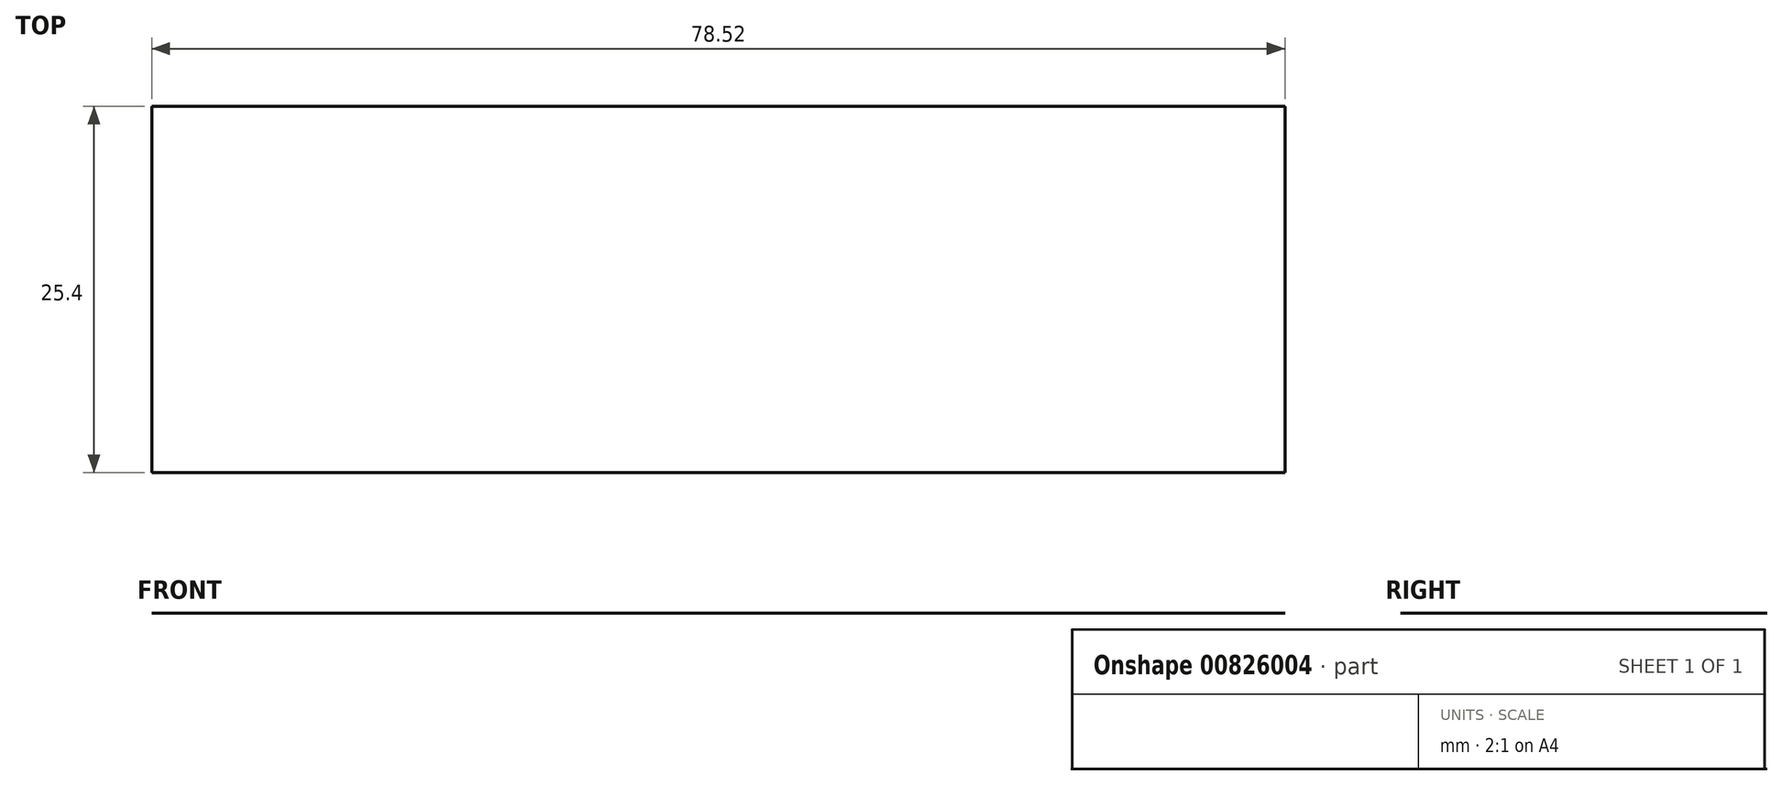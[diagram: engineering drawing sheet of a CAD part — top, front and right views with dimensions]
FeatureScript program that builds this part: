
annotation { "Feature Type Name" : "Feature", "Feature Type Description" : "" }
export const myFeature = defineFeature(function(context is Context, id is Id, definition is map)
    precondition{}
    {
        {
            var Q0;
            Q0=qCreatedBy(makeId("Front.planeOp"),FACE);
            var sketch = newSketch(context, id + "F0", { "sketchPlane" : qUnion([Q0])});
            skLineSegment(sketch, "E0.bottom", {"start": v(0, 0) * mm, "end": v(-78.52, 0) * mm});
            skLineSegment(sketch, "E0.top", {"start": v(0, -67.9) * mm, "end": v(-78.52, -67.9) * mm});
            skLineSegment(sketch, "E0.left", {"start": v(0, 0) * mm, "end": v(0, -67.9) * mm});
            skLineSegment(sketch, "E0.right", {"start": v(-78.52, 0) * mm, "end": v(-78.52, -67.9) * mm});
            skSolve(sketch);
        }
        {
            var Q0;
            Q0=sQuery(id+"F0.wireOp",EDGE,"E0.bottom");
            extrude(context, id + "F1", {"bodyType" : ToolBodyType.SURFACE, "surfaceEntities" : qUnion([Q0]), "depth" : 25.4 * mm, "offsetDistance" : 25.4 * mm});
        }
    });
